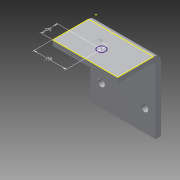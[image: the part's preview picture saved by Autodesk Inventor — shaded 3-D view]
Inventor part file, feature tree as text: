
AUTODESK INVENTOR PART (.ipt)
format: ipt  version: 2014 (Build 180170000, 170)  size: 108,544 bytes
history: native  units: in
note: dims shown in document units (in); Inventor stores cm internally (conversion verified against a paired STEP export)
features: sheet_metal_op x4, sketch x3, other x2
ambient origin geometry x8: Origin, YZ Plane, XZ Plane, XY Plane, X Axis, Y Axis, Z Axis, Center Point
bodies: Solid1 (feature_tree)
feature tree (9):
  sheet_metal_op  "Face1"
  sheet_metal_op  "Flange1"
  sketch  "Sketch3"  dims[d2=0.163in d3=0.25in d4=0.7874in d6=1.0in d7=0.3937in d9=1.0in d11=0.125in d12=0.125in d13=0.0625in d14=0.25in d15=0.125in d16=1.0in d17=90.0deg d18=0.05in d19=0.5in d20=0.125in d21=0.125in d22=0.5in d23=0.185in d24=0.375in d25=0.75in]
  sketch  "Sketch1"  dims[d0=1.5in]
  other  "Plate1"
  sketch  "Sketch2"  dims[d1=1.5in]
  other  "Plate2"
  sheet_metal_op  "Bend1"
  sheet_metal_op  "Corner1"
